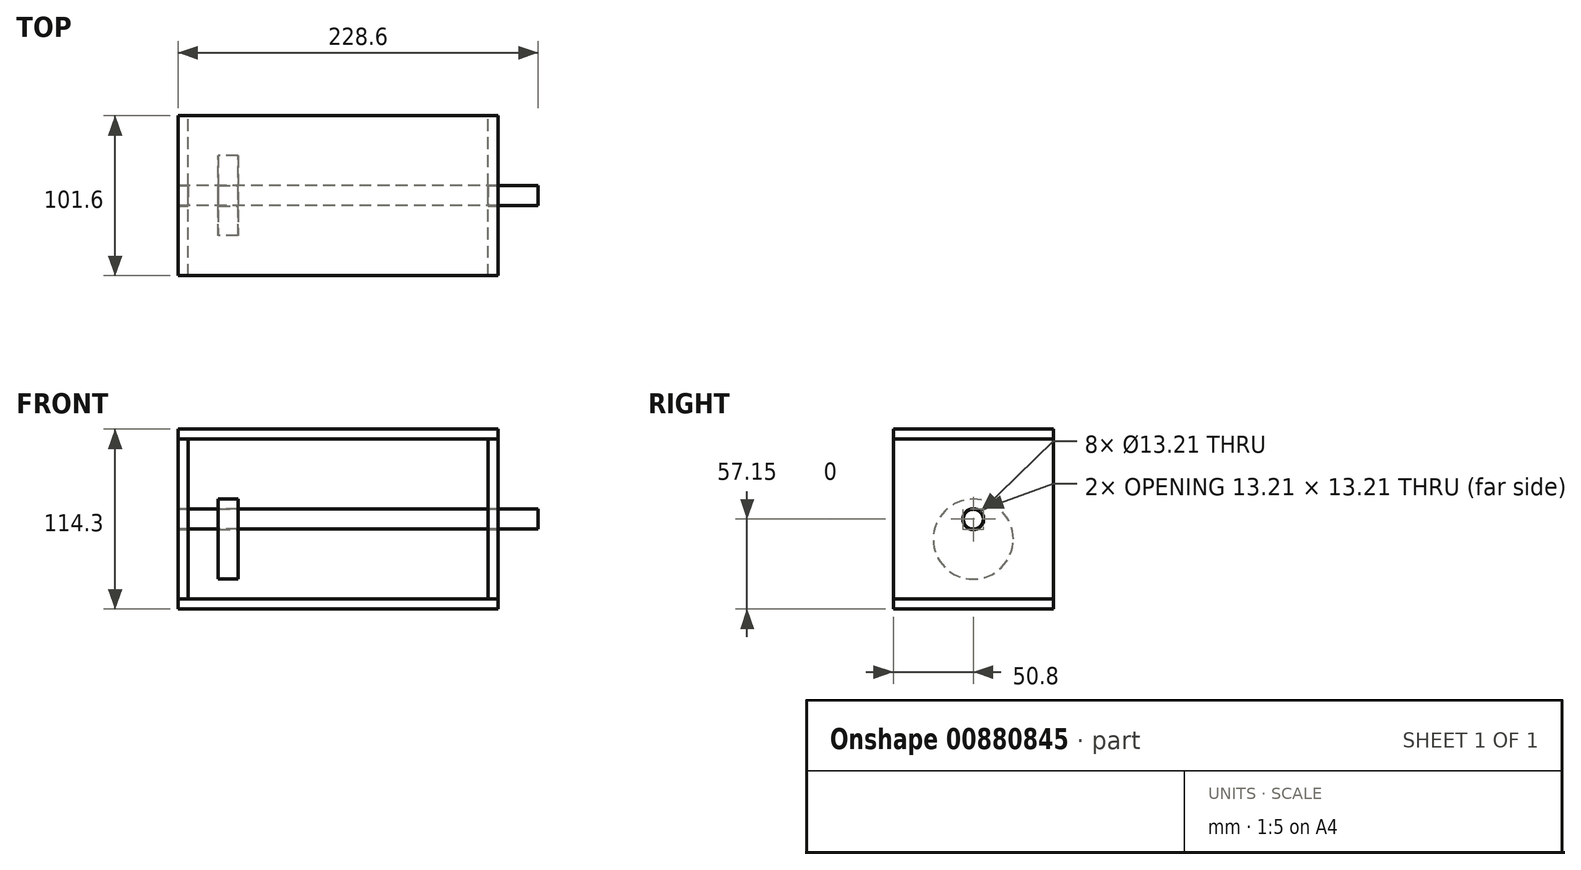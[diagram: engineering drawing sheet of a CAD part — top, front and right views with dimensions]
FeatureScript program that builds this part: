
annotation { "Feature Type Name" : "Feature", "Feature Type Description" : "" }
export const myFeature = defineFeature(function(context is Context, id is Id, definition is map)
    precondition{}
    {
        {
            var Q0;
            Q0=qCreatedBy(makeId("Front.planeOp"),FACE);
            var sketch = newSketch(context, id + "F0", { "sketchPlane" : qUnion([Q0])});
            skLineSegment(sketch, "E0", {"start": v(-101.6, 0) * mm, "end": v(101.6, 0) * mm});
            skLineSegment(sketch, "E1", {"start": v(-101.6, 6.35) * mm, "end": v(101.6, 6.35) * mm});
            skLineSegment(sketch, "E2", {"start": v(-101.6, 0) * mm, "end": v(-101.6, 6.35) * mm});
            skLineSegment(sketch, "E3", {"start": v(101.6, 0) * mm, "end": v(101.6, 6.35) * mm});
            skLineSegment(sketch, "E4", {"start": v(-101.6, 6.35) * mm, "end": v(-101.6, 107.95) * mm});
            skLineSegment(sketch, "E5", {"start": v(101.6, 6.35) * mm, "end": v(101.6, 107.95) * mm});
            skLineSegment(sketch, "E6.bottom", {"start": v(-101.6, 107.95) * mm, "end": v(101.6, 107.95) * mm});
            skLineSegment(sketch, "E6.top", {"start": v(-101.6, 114.3) * mm, "end": v(101.6, 114.3) * mm});
            skLineSegment(sketch, "E6.left", {"start": v(-101.6, 107.95) * mm, "end": v(-101.6, 114.3) * mm});
            skLineSegment(sketch, "E6.right", {"start": v(101.6, 107.95) * mm, "end": v(101.6, 114.3) * mm});
            skLineSegment(sketch, "E7", {"start": v(-95.25, 107.95) * mm, "end": v(-95.25, 6.35) * mm});
            skLineSegment(sketch, "E8", {"start": v(95.25, 107.95) * mm, "end": v(95.25, 6.35) * mm});
            skLineSegment(sketch, "E9", {"start": v(95.25, 57.15) * mm, "end": v(101.6, 57.15) * mm, "construction": true});
            skLineSegment(sketch, "E10", {"start": v(-101.6, 57.15) * mm, "end": v(-95.25, 57.15) * mm, "construction": true});
            skLineSegment(sketch, "E11", {"start": v(-95.25, 57.15) * mm, "end": v(95.25, 57.15) * mm});
            skLineSegment(sketch, "E12.bottom", {"start": v(-76.2, 69.85) * mm, "end": v(-63.5, 69.85) * mm});
            skLineSegment(sketch, "E12.top", {"start": v(-76.2, 19.05) * mm, "end": v(-63.5, 19.05) * mm});
            skLineSegment(sketch, "E12.right", {"start": v(-63.5, 69.85) * mm, "end": v(-63.5, 19.05) * mm});
            skLineSegment(sketch, "E13.bottom", {"start": v(-6.35, 88.9) * mm, "end": v(6.35, 88.9) * mm});
            skLineSegment(sketch, "E13.top", {"start": v(-6.35, 38.1) * mm, "end": v(6.35, 38.1) * mm});
            skLineSegment(sketch, "E13.left", {"start": v(-6.35, 88.9) * mm, "end": v(-6.35, 38.1) * mm});
            skLineSegment(sketch, "E13.right", {"start": v(6.35, 88.9) * mm, "end": v(6.35, 38.1) * mm});
            skLineSegment(sketch, "E14.bottom", {"start": v(63.5, 88.9) * mm, "end": v(76.2, 88.9) * mm});
            skLineSegment(sketch, "E14.top", {"start": v(63.5, 38.1) * mm, "end": v(76.2, 38.1) * mm});
            skLineSegment(sketch, "E14.left", {"start": v(63.5, 88.9) * mm, "end": v(63.5, 38.1) * mm});
            skLineSegment(sketch, "E14.right", {"start": v(76.2, 88.9) * mm, "end": v(76.2, 38.1) * mm});
            skLineSegment(sketch, "E15.left", {"start": v(-76.2, 69.85) * mm, "end": v(-76.2, 69.85) * mm});
            skLineSegment(sketch, "E15.right", {"start": v(-63.5, 69.85) * mm, "end": v(-63.5, 69.85) * mm});
            skLineSegment(sketch, "E16.bottom", {"start": v(-76.2, 19.05) * mm, "end": v(-76.2, 69.85) * mm});
            skLineSegment(sketch, "E17", {"start": v(-76.2, 44.45) * mm, "end": v(-63.5, 44.45) * mm});
            skLineSegment(sketch, "E18", {"start": v(-6.35, 63.5) * mm, "end": v(6.35, 63.5) * mm});
            skLineSegment(sketch, "E19", {"start": v(63.5, 63.5) * mm, "end": v(76.2, 63.5) * mm});
            skLineSegment(sketch, "E20", {"start": v(0, 63.5) * mm, "end": v(0, 57.15) * mm, "construction": true});
            skLineSegment(sketch, "E21", {"start": v(69.85, 63.5) * mm, "end": v(69.85, 57.15) * mm, "construction": true});
            skLineSegment(sketch, "E22", {"start": v(-69.85, 44.45) * mm, "end": v(-69.85, 57.15) * mm, "construction": true});
            skSolve(sketch);
        }
        {
            var Q0;
            Q0=makeQuery(id+"F0.imprint","IMPRINT",FACE,{"disambiguationData":[TD([[makeQuery(id+"F0.imprint","IMPRINT",EDGE,{"derivedFrom":sQuery(id+"F0.wireOp",EDGE,"E0")}),1.0]])]});
            var Q1;
            Q1=makeQuery(id+"F0.imprint","IMPRINT",FACE,{"disambiguationData":[TD([[makeQuery(id+"F0.imprint","IMPRINT",EDGE,{"derivedFrom":sQuery(id+"F0.wireOp",EDGE,"E6.top")}),-1.0]])]});
            extrude(context, id + "F1", {"entities" : qUnion([Q0, Q1]), "endBound" : BoundingType.SYMMETRIC, "depth" : 101.6 * mm, "offsetDistance" : 25.4 * mm});
        }
        {
            var Q0;
            {var subQ4=sQuery(id+"F0.wireOp",EDGE,"E4");Q0=makeQuery(id+"F0.imprint","IMPRINT",FACE,{"disambiguationData":[TD([[makeQuery(id+"F0.imprint","IMPRINT",EDGE,{"derivedFrom":subQ4}),-1.0]])]});}
            var Q1;
            {var subQ4=sQuery(id+"F0.wireOp",EDGE,"E5");Q1=makeQuery(id+"F0.imprint","IMPRINT",FACE,{"disambiguationData":[TD([[makeQuery(id+"F0.imprint","IMPRINT",EDGE,{"derivedFrom":subQ4}),1.0]])]});}
            var Q2;
            Q2=makeQuery(id+"F1.opExtrude","CAP_FACE",FACE,{"disambiguationData":[OSD([sQuery(id+"F0.wireOp",EDGE,"E6.bottom"),sQuery(id+"F0.wireOp",EDGE,"E6.top"),sQuery(id+"F0.wireOp",EDGE,"E6.left"),sQuery(id+"F0.wireOp",EDGE,"E6.right")])],"isStart":false});
            var Q3;
            Q3=makeQuery(id+"F1.opExtrude","CAP_FACE",FACE,{"disambiguationData":[OSD([sQuery(id+"F0.wireOp",EDGE,"E6.bottom"),sQuery(id+"F0.wireOp",EDGE,"E6.top"),sQuery(id+"F0.wireOp",EDGE,"E6.left"),sQuery(id+"F0.wireOp",EDGE,"E6.right")])],"isStart":true});
            extrude(context, id + "F2", {"entities" : qUnion([Q0, Q1]), "endBound" : BoundingType.UP_TO_SURFACE, "depth" : 25.4 * mm, "endBoundEntityFace" : qUnion([Q2]), "offsetDistance" : 25.4 * mm, "hasSecondDirection" : true, "secondDirectionBound" : SecondDirectionBoundingType.UP_TO_SURFACE, "secondDirectionOppositeDirection" : true, "secondDirectionDepth" : 25.4 * mm, "secondDirectionBoundEntityFace" : qUnion([Q3])});
        }
        {
            var Q0;
            Q0=makeQuery(id+"F2.opExtrude","SWEPT_FACE",FACE,{"disambiguationData":[OSD([sQuery(id+"F0.wireOp",EDGE,"E5")])]});
            var sketch = newSketch(context, id + "F3", { "sketchPlane" : qUnion([Q0])});
            skCircle(sketch, "E23", {"center": v(0, 57.15) * mm, "radius": 6.35 * mm});
            skPoint(sketch, "E23.centerSnap0", {"position": v(50.8, 57.15) * mm});
            skCircle(sketch, "E24", {"center": v(0, 57.15) * mm, "radius": 6.6 * mm});
            skSolve(sketch);
        }
        {
            var Q0;
            Q0=makeQuery(id+"F3.imprint","IMPRINT",FACE,{"disambiguationData":[TD([[makeQuery(id+"F3.imprint","IMPRINT",EDGE,{"derivedFrom":sQuery(id+"F3.wireOp",EDGE,"E23")}),1.0]])]});
            var Q1;
            Q1=makeQuery(id+"F3.imprint","IMPRINT",FACE,{"disambiguationData":[TD([[makeQuery(id+"F3.imprint","IMPRINT",EDGE,{"derivedFrom":sQuery(id+"F3.wireOp",EDGE,"E23")}),-1.0]])]});
            extrude(context, id + "F4", {"entities" : qUnion([Q0, Q1]), "operationType" : NewBodyOperationType.REMOVE, "endBound" : BoundingType.THROUGH_ALL, "oppositeDirection" : true, "depth" : 25.4 * mm, "offsetDistance" : 25.4 * mm});
        }
        {
            var Q0;
            Q0=makeQuery(id+"F3.imprint","IMPRINT",FACE,{"disambiguationData":[TD([[makeQuery(id+"F3.imprint","IMPRINT",EDGE,{"derivedFrom":sQuery(id+"F3.wireOp",EDGE,"E23")}),1.0]])]});
            var Q1;
            Q1=makeQuery(id+"F2.opExtrude","SWEPT_FACE",FACE,{"disambiguationData":[OSD([sQuery(id+"F0.wireOp",EDGE,"E4")])]});
            extrude(context, id + "F5", {"entities" : qUnion([Q0]), "depth" : 25.4 * mm, "offsetDistance" : 25.4 * mm, "hasSecondDirection" : true, "secondDirectionBound" : SecondDirectionBoundingType.UP_TO_SURFACE, "secondDirectionOppositeDirection" : true, "secondDirectionDepth" : 25.4 * mm, "secondDirectionBoundEntityFace" : qUnion([Q1])});
        }
        {
            var Q0;
            {var subQ0=sQuery(id+"F0.wireOp",EDGE,"E12.top");Q0=makeQuery(id+"F0.imprint","IMPRINT",FACE,{"disambiguationData":[TD([[makeQuery(id+"F0.imprint","IMPRINT",EDGE,{"derivedFrom":subQ0}),1.0]])]});}
            var Q1;
            Q1=sQuery(id+"F0.wireOp",EDGE,"E17");
            revolve(context, id + "F6", {"surfaceOperationType" : NewSurfaceOperationType.NEW, "entities" : qUnion([Q0]), "axis" : qUnion([Q1]), "revolveType" : RevolveType.FULL});
        }
    });
